# Revit family: TYCO-FPP-Zettler-LIM800 Ancillary line isolator module
name_source: partatom
category: Electrical Fixtures
revit_build: Autodesk Revit 2014 (Build: 20130308_1515(x64)
units: mm (PartAtom-declared; Revit-internal decimal feet)

## types (1)
- TYCO-FPP-Zettler-LIM800 Ancillary line isolator module
    Ambient Temperature = –25°C to +70°C
    Description = The LIM800 is an MX Addressable Loop Isolator Module
that can be used to provide short circuit isolation between
zones or portions of the MX addressable loop.
    Equivalent Capacitance = 0.5nF
    Front Cover = Yes
    Input Current = 80μA
    Keynote = LED indication of LIM800 operation
    Length = 61 mm
    Loop Voltage = 20V to 40Vdc
    Manufacturer = Tyco
    Model = Zettler - 545.800.004
    PCB = PCB
    Rear Cover = Yes
    Relative Humidity = 10% to 95%
    Series Resistance (max.) = 0.25 Ohm
    Storage Temperature = –40°C to +80°C
    Thickness = 3 mm
    Type Comments = Automatic short-circuit protection for the
MX Addressable Loop
    URL = https://www.tycosafetyproducts-anz.com
    Width = 84 mm
    Wire Size (maximum) = 2.5sq. mm

## geometry (parser evidence)
native form markers: Sweep x8
no freeform markers — native parametric forms only
